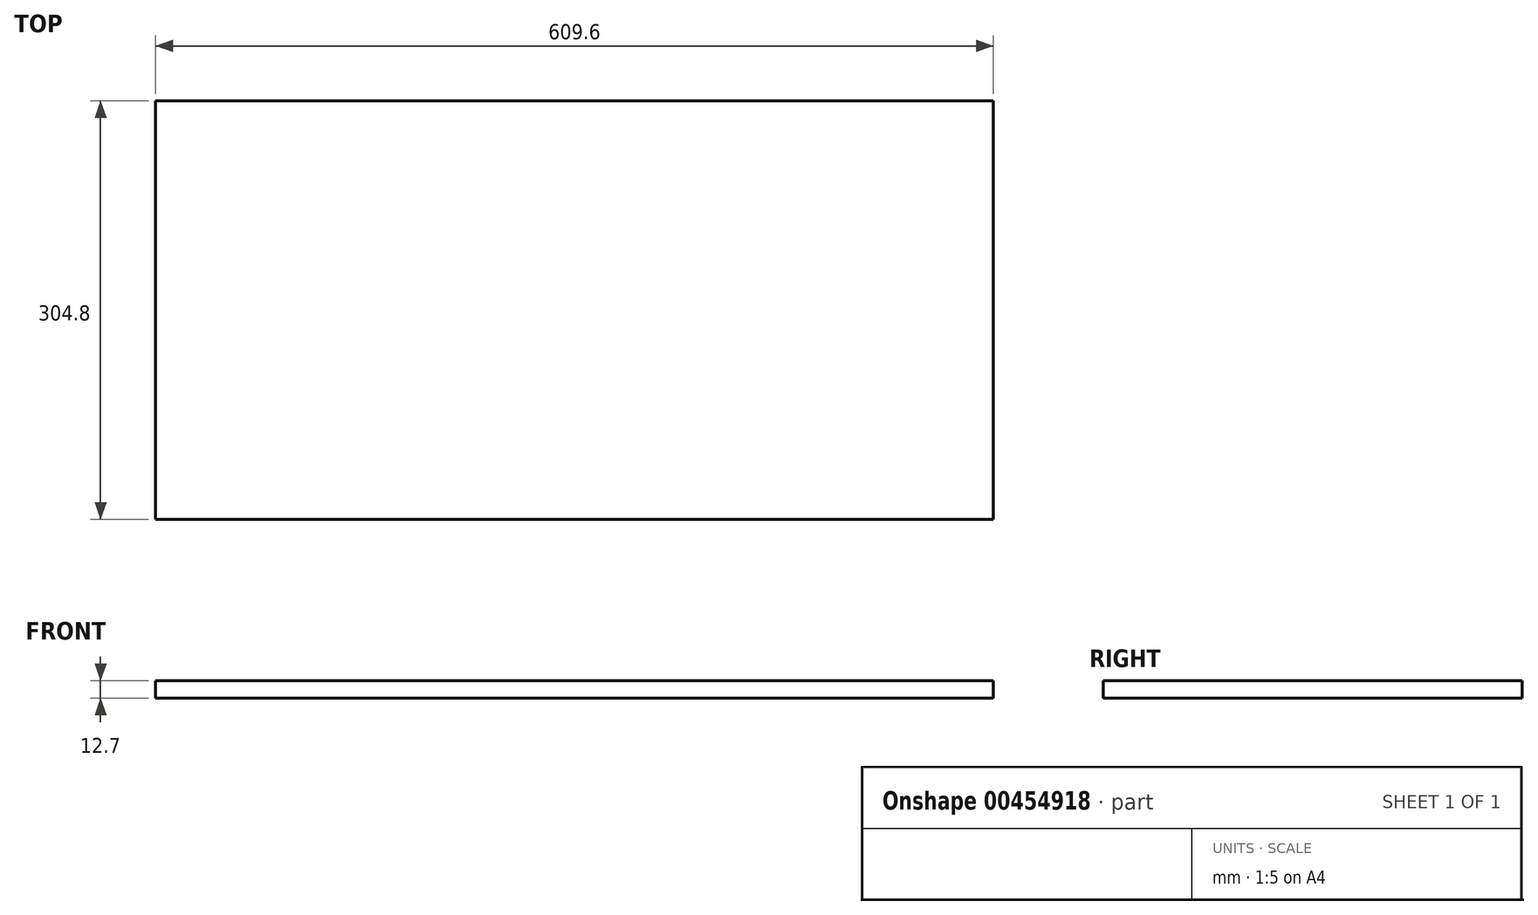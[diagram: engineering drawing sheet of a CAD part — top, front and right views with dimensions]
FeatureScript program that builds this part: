
annotation { "Feature Type Name" : "Feature", "Feature Type Description" : "" }
export const myFeature = defineFeature(function(context is Context, id is Id, definition is map)
    precondition{}
    {
        {
            var Q0;
            Q0=qCreatedBy(makeId("Top.planeOp"),FACE);
            var sketch = newSketch(context, id + "F0", { "sketchPlane" : qUnion([Q0])});
            skLineSegment(sketch, "E0.bottom", {"start": v(0, 0) * mm, "end": v(609.6, 0) * mm});
            skLineSegment(sketch, "E0.top", {"start": v(0, 304.8) * mm, "end": v(609.6, 304.8) * mm});
            skLineSegment(sketch, "E0.left", {"start": v(0, 0) * mm, "end": v(0, 304.8) * mm});
            skLineSegment(sketch, "E0.right", {"start": v(609.6, 0) * mm, "end": v(609.6, 304.8) * mm});
            skSolve(sketch);
        }
        {
            var Q0;
            Q0 = qSketchRegion(id + "F0", true);
            extrude(context, id + "F1", {"entities" : qUnion([Q0]), "depth" : 12.7 * mm});
        }
    });
